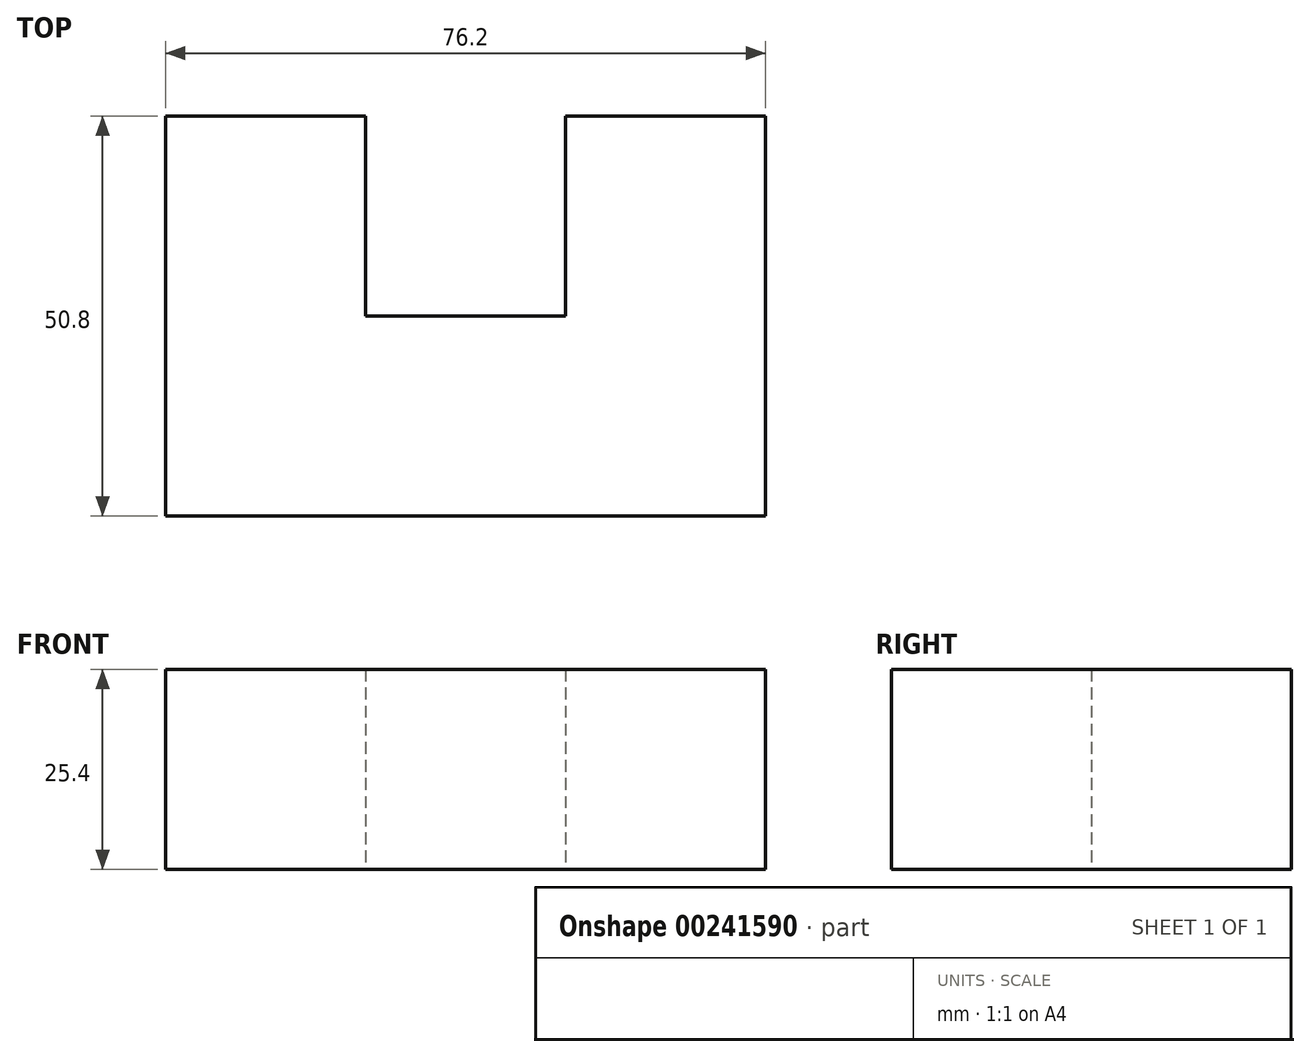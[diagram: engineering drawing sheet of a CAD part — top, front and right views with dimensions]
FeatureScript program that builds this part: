
annotation { "Feature Type Name" : "Feature", "Feature Type Description" : "" }
export const myFeature = defineFeature(function(context is Context, id is Id, definition is map)
    precondition{}
    {
        {
            var Q0;
            Q0=qCreatedBy(makeId("Front.planeOp"),FACE);
            var sketch = newSketch(context, id + "F0", { "sketchPlane" : qUnion([Q0])});
            skLineSegment(sketch, "E0.bottom", {"start": v(-33.7, 7.6) * mm, "end": v(42.5, 7.6) * mm});
            skLineSegment(sketch, "E0.top", {"start": v(-33.7, -17.8) * mm, "end": v(42.5, -17.8) * mm});
            skLineSegment(sketch, "E0.left", {"start": v(-33.7, 7.6) * mm, "end": v(-33.7, -17.8) * mm});
            skLineSegment(sketch, "E0.right", {"start": v(42.5, 7.6) * mm, "end": v(42.5, -17.8) * mm});
            skSolve(sketch);
        }
        {
            var Q0;
            Q0=makeQuery(id+"F0.imprint","IMPRINT",FACE,{"disambiguationData":[TD([[makeQuery(id+"F0.imprint","IMPRINT",EDGE,{"derivedFrom":sQuery(id+"F0.wireOp",EDGE,"E0.bottom")}),-1.0]])]});
            extrude(context, id + "F1", {"entities" : qUnion([Q0]), "depth" : 25.4 * mm});
        }
        {
            var Q0;
            Q0=makeQuery(id+"F1.opExtrude","CAP_FACE",FACE,{"disambiguationData":[OSD([sQuery(id+"F0.wireOp",EDGE,"E0.bottom"),sQuery(id+"F0.wireOp",EDGE,"E0.top"),sQuery(id+"F0.wireOp",EDGE,"E0.left"),sQuery(id+"F0.wireOp",EDGE,"E0.right")])],"isStart":true});
            var sketch = newSketch(context, id + "F2", { "sketchPlane" : qUnion([Q0])});
            skLineSegment(sketch, "E1.bottom", {"start": v(-17.1, 7.6) * mm, "end": v(-42.5, 7.6) * mm});
            skLineSegment(sketch, "E1.top", {"start": v(-17.1, -17.8) * mm, "end": v(-42.5, -17.8) * mm});
            skLineSegment(sketch, "E1.left", {"start": v(-17.1, 7.6) * mm, "end": v(-17.1, -17.8) * mm});
            skLineSegment(sketch, "E1.right", {"start": v(-42.5, 7.6) * mm, "end": v(-42.5, -17.8) * mm});
            skSolve(sketch);
        }
        {
            var Q0;
            Q0=makeQuery(id+"F2.imprint","IMPRINT",FACE,{"disambiguationData":[TD([[makeQuery(id+"F2.imprint","IMPRINT",EDGE,{"derivedFrom":sQuery(id+"F2.wireOp",EDGE,"E1.bottom")}),1.0]])]});
            extrude(context, id + "F3", {"entities" : qUnion([Q0]), "operationType" : NewBodyOperationType.ADD, "depth" : 25.4 * mm});
        }
        {
            var Q0;
            Q0=makeQuery(id+"F1.opExtrude","CAP_FACE",FACE,{"disambiguationData":[OSD([sQuery(id+"F0.wireOp",EDGE,"E0.bottom"),sQuery(id+"F0.wireOp",EDGE,"E0.top"),sQuery(id+"F0.wireOp",EDGE,"E0.left"),sQuery(id+"F0.wireOp",EDGE,"E0.right")])],"isStart":true});
            var sketch = newSketch(context, id + "F4", { "sketchPlane" : qUnion([Q0])});
            skLineSegment(sketch, "E2.bottom", {"start": v(8.3, 7.6) * mm, "end": v(33.7, 7.6) * mm});
            skLineSegment(sketch, "E2.top", {"start": v(8.3, -17.8) * mm, "end": v(33.7, -17.8) * mm});
            skLineSegment(sketch, "E2.left", {"start": v(8.3, 7.6) * mm, "end": v(8.3, -17.8) * mm});
            skLineSegment(sketch, "E2.right", {"start": v(33.7, 7.6) * mm, "end": v(33.7, -17.8) * mm});
            skSolve(sketch);
        }
        {
            var Q0;
            Q0=makeQuery(id+"F4.imprint","IMPRINT",FACE,{"disambiguationData":[TD([[makeQuery(id+"F4.imprint","IMPRINT",EDGE,{"derivedFrom":sQuery(id+"F4.wireOp",EDGE,"E2.bottom")}),1.0]])]});
            extrude(context, id + "F5", {"entities" : qUnion([Q0]), "operationType" : NewBodyOperationType.ADD, "depth" : 25.4 * mm});
        }
    });
